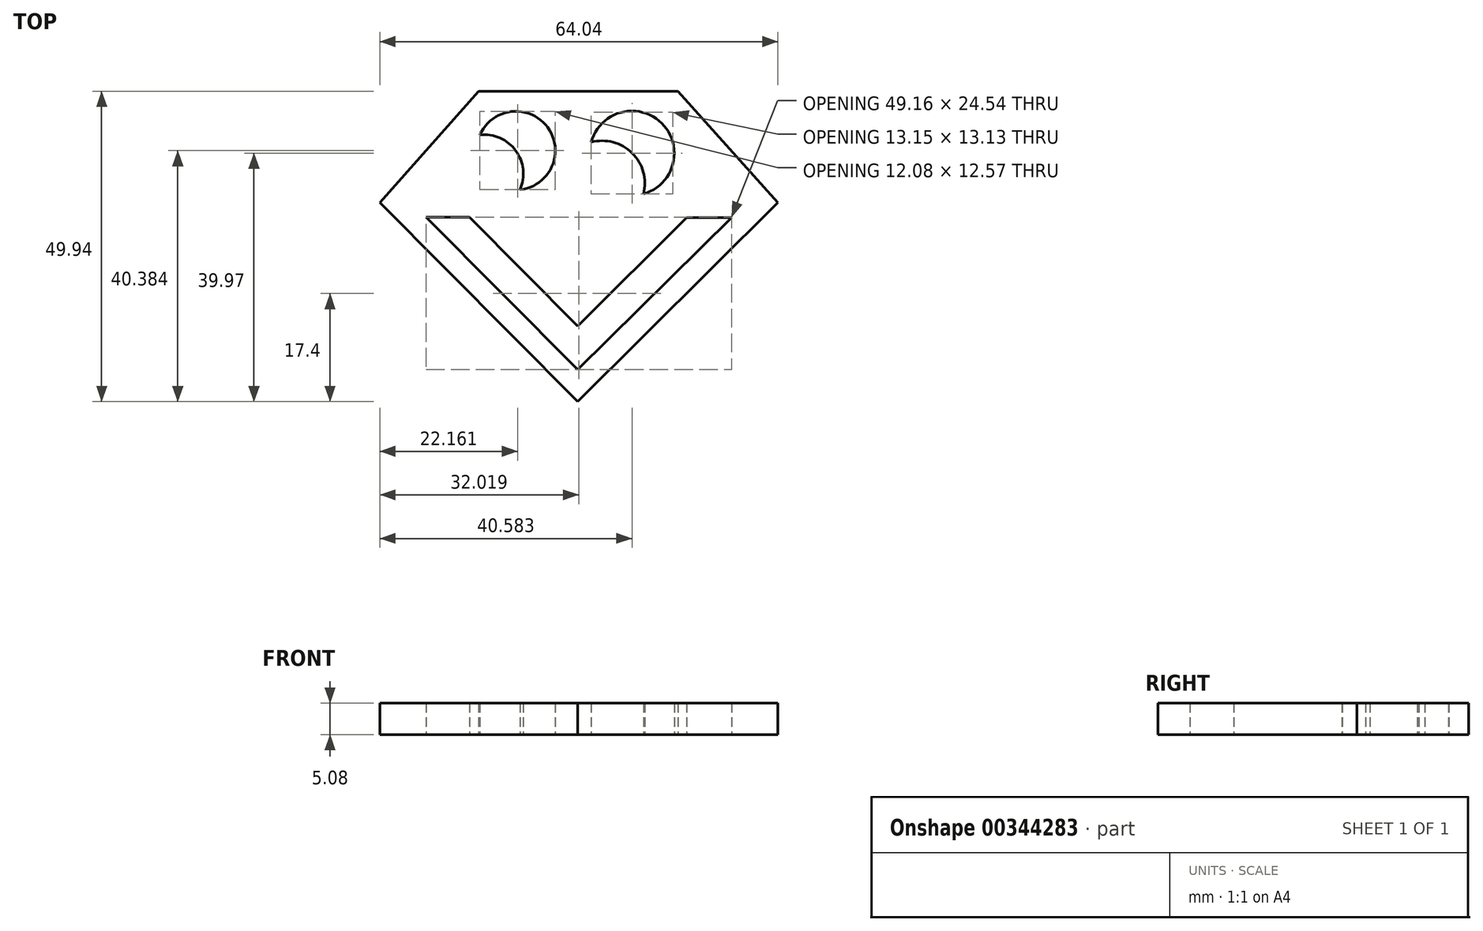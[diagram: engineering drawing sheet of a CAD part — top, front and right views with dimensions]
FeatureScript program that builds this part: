
annotation { "Feature Type Name" : "Feature", "Feature Type Description" : "" }
export const myFeature = defineFeature(function(context is Context, id is Id, definition is map)
    precondition{}
    {
        {
            var Q0;
            Q0=qCreatedBy(makeId("Top.planeOp"),FACE);
            var sketch = newSketch(context, id + "F0", { "sketchPlane" : qUnion([Q0])});
            skLineSegment(sketch, "E0", {"start": v(-15.92, 17.92) * mm, "end": v(-31.85, 0) * mm});
            skLineSegment(sketch, "E1", {"start": v(-31.85, 0) * mm, "end": v(0, -32.02) * mm});
            skLineSegment(sketch, "E2", {"start": v(0, -32.02) * mm, "end": v(32.19, 0) * mm});
            skLineSegment(sketch, "E3", {"start": v(32.19, 0) * mm, "end": v(16.1, 17.92) * mm});
            skLineSegment(sketch, "E4", {"start": v(-24.4, -2.35) * mm, "end": v(0, -26.89) * mm});
            skLineSegment(sketch, "E5", {"start": v(0, -19.85) * mm, "end": v(-17.4, -2.36) * mm});
            skLineSegment(sketch, "E6", {"start": v(-17.4, -2.36) * mm, "end": v(-24.4, -2.35) * mm});
            skLineSegment(sketch, "E7", {"start": v(17.53, -2.41) * mm, "end": v(24.75, -2.43) * mm});
            skLineSegment(sketch, "E8", {"start": v(24.75, -2.43) * mm, "end": v(0, -26.89) * mm});
            skLineSegment(sketch, "E9", {"start": v(0, -19.85) * mm, "end": v(17.53, -2.41) * mm});
            skLineSegment(sketch, "E10", {"start": v(-15.92, 17.92) * mm, "end": v(16.1, 17.92) * mm});
            skPoint(sketch, "E11.orphan", {"position": v(0, 35.83) * mm});
            skArc(sketch, "E12", {"start": v(-9.29, 2.08) * mm, "mid": v(-4.83, 12.1) * mm, "end": v(-15.73, 10.88) * mm});
            skArc(sketch, "E13", {"start": v(10.56, 1.39) * mm, "mid": v(13.51, 12.77) * mm, "end": v(2.16, 9.71) * mm});
            skArc(sketch, "E14", {"start": v(-9.29, 2.08) * mm, "mid": v(-9.96, 8.35) * mm, "end": v(-15.73, 10.88) * mm});
            skArc(sketch, "E15", {"start": v(10.56, 1.39) * mm, "mid": v(8.75, 7.97) * mm, "end": v(2.16, 9.71) * mm});
            skSolve(sketch);
        }
        {
            var Q0;
            Q0 = qSketchRegion(id + "F0", true);
            extrude(context, id + "F1", {"entities" : qUnion([Q0]), "depth" : 5.08 * mm});
        }
    });
